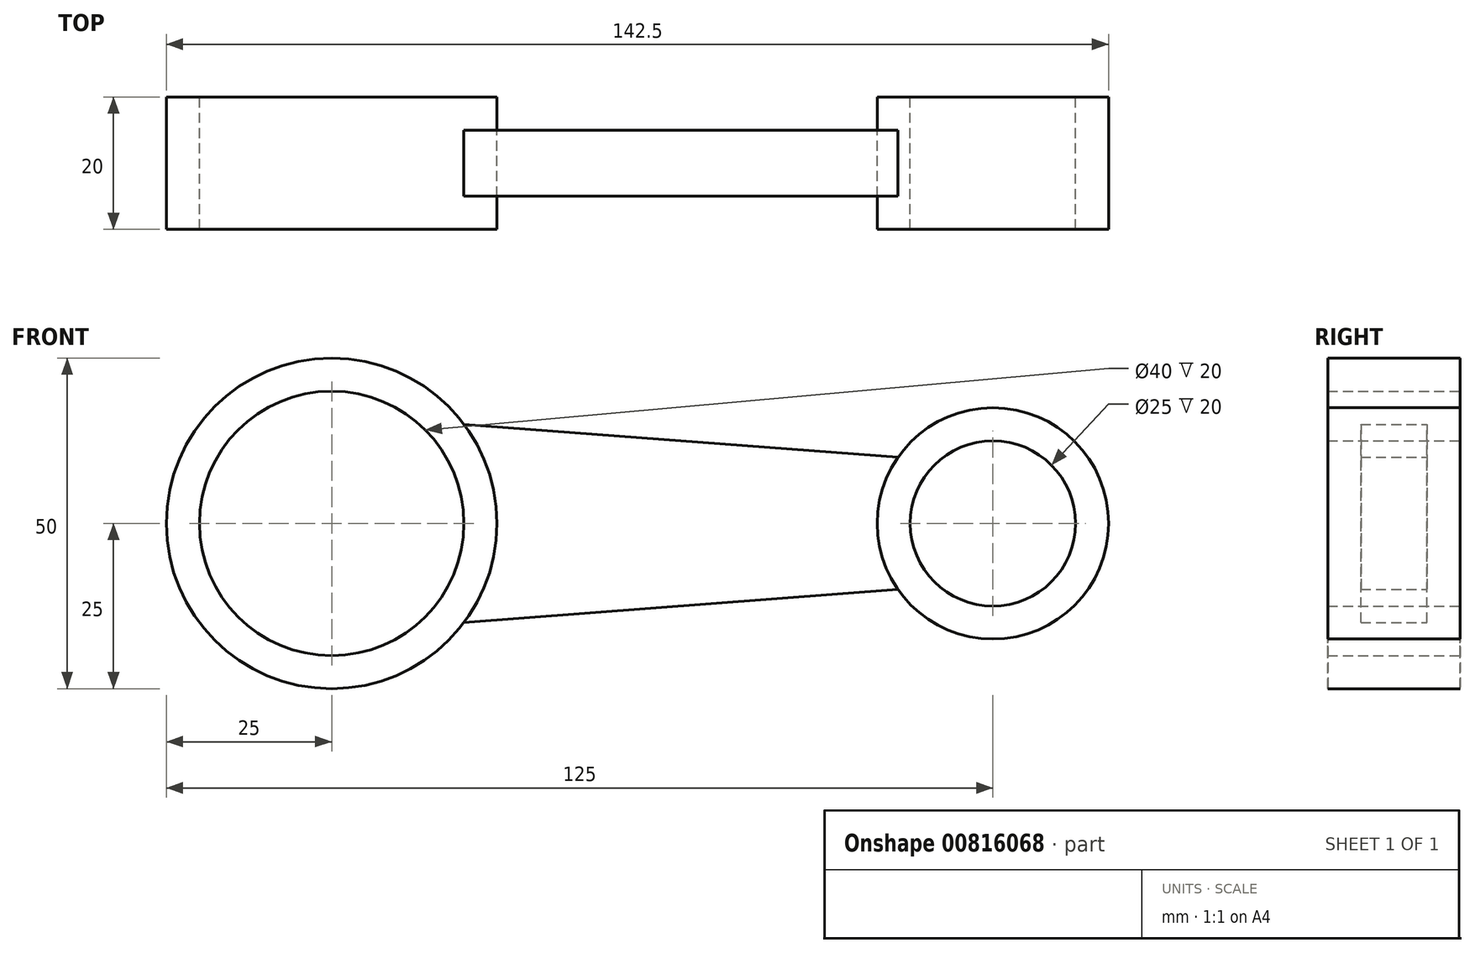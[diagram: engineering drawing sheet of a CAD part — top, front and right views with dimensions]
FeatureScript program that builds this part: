
annotation { "Feature Type Name" : "Feature", "Feature Type Description" : "" }
export const myFeature = defineFeature(function(context is Context, id is Id, definition is map)
    precondition{}
    {
        {
            var Q0;
            Q0=qCreatedBy(makeId("Front.planeOp"),FACE);
            var sketch = newSketch(context, id + "F0", { "sketchPlane" : qUnion([Q0])});
            skCircle(sketch, "E0", {"center": v(0, 0) * mm, "radius": 25 * mm});
            skCircle(sketch, "E1", {"center": v(0, 0) * mm, "radius": 20 * mm});
            skLineSegment(sketch, "E2", {"start": v(0, 0) * mm, "end": v(100, 0) * mm, "construction": true});
            skCircle(sketch, "E3", {"center": v(100, 0) * mm, "radius": 17.5 * mm});
            skCircle(sketch, "E4", {"center": v(100, 0) * mm, "radius": 12.5 * mm});
            skLineSegment(sketch, "E5", {"start": v(20, 15) * mm, "end": v(85.64, 10) * mm});
            skLineSegment(sketch, "E6.MirrorCS", {"start": v(20, -15) * mm, "end": v(85.64, -10) * mm});
            skSolve(sketch);
        }
        {
            var Q0;
            Q0=makeQuery(id+"F0.imprint","IMPRINT",FACE,{"disambiguationData":[TD([[makeQuery(id+"F0.imprint","IMPRINT",EDGE,{"derivedFrom":sQuery(id+"F0.wireOp",EDGE,"E0")}),1.0]])]});
            var Q1;
            Q1=makeQuery(id+"F0.imprint","IMPRINT",FACE,{"disambiguationData":[TD([[makeQuery(id+"F0.imprint","IMPRINT",EDGE,{"derivedFrom":sQuery(id+"F0.wireOp",EDGE,"E3")}),1.0]])]});
            extrude(context, id + "F1", {"entities" : qUnion([Q0, Q1]), "endBound" : BoundingType.SYMMETRIC, "depth" : 20 * mm, "offsetDistance" : 25 * mm});
        }
        {
            var Q0;
            {var subQ0=sQuery(id+"F0.wireOp",EDGE,"E5");Q0=makeQuery(id+"F0.imprint","IMPRINT",FACE,{"disambiguationData":[TD([[makeQuery(id+"F0.imprint","IMPRINT",EDGE,{"derivedFrom":subQ0}),-1.0]])]});}
            extrude(context, id + "F2", {"entities" : qUnion([Q0]), "endBound" : BoundingType.SYMMETRIC, "depth" : 10 * mm, "offsetDistance" : 25 * mm});
        }
    });
